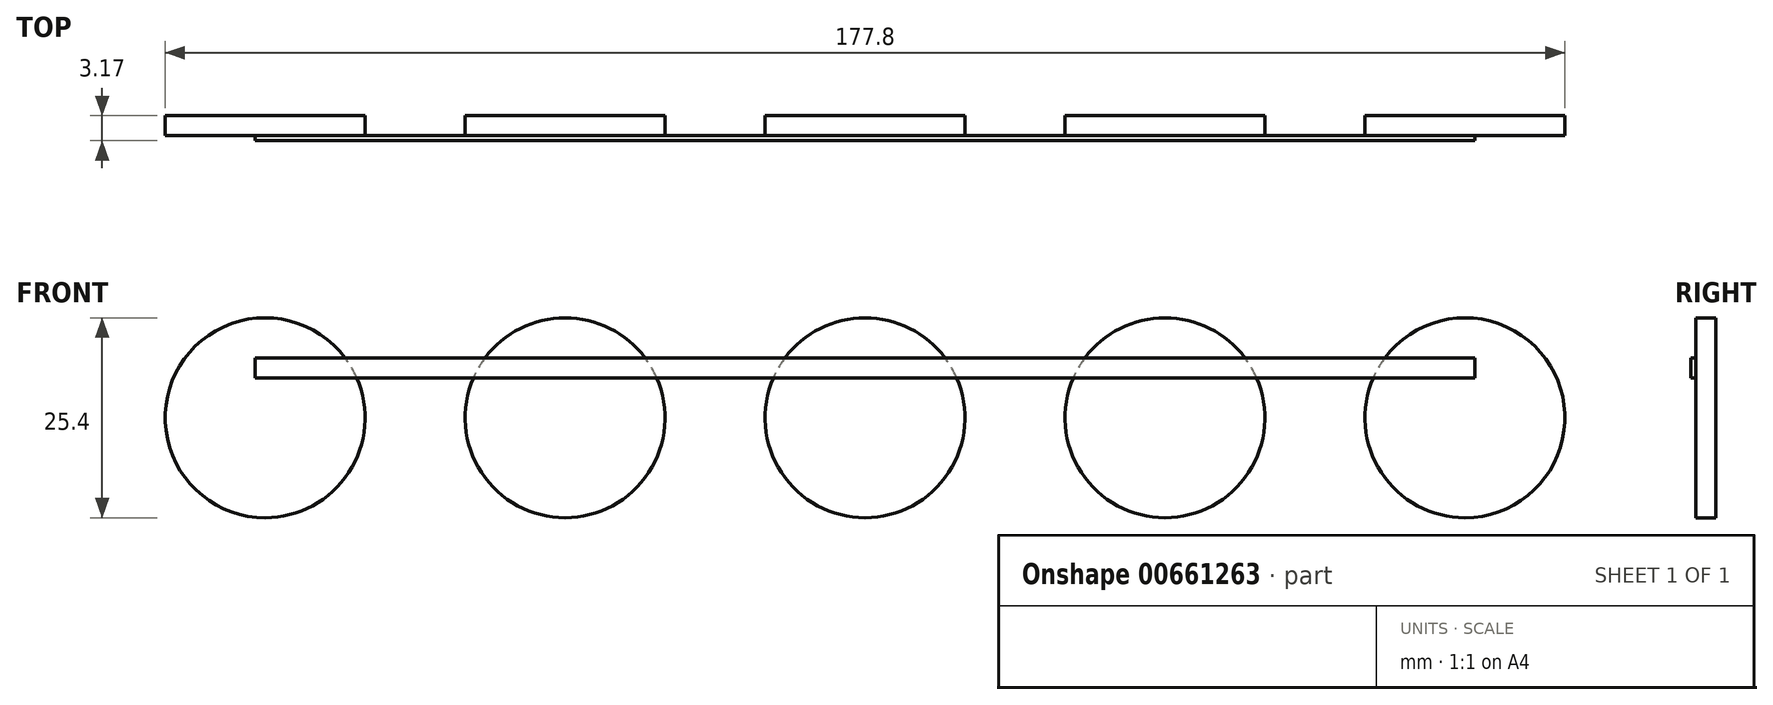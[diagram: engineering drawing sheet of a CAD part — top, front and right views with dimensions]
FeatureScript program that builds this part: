
annotation { "Feature Type Name" : "Feature", "Feature Type Description" : "" }
export const myFeature = defineFeature(function(context is Context, id is Id, definition is map)
    precondition{}
    {
        {
            var Q0;
            Q0=qCreatedBy(makeId("Front.planeOp"),FACE);
            var sketch = newSketch(context, id + "F0", { "sketchPlane" : qUnion([Q0])});
            skCircle(sketch, "E0", {"center": v(0, 0) * mm, "radius": 12.7 * mm});
            skCircle(sketch, "E1", {"center": v(38.1, 0) * mm, "radius": 12.7 * mm});
            skCircle(sketch, "E2", {"center": v(76.2, 0) * mm, "radius": 12.7 * mm});
            skCircle(sketch, "E3", {"center": v(-38.1, 0) * mm, "radius": 12.7 * mm});
            skCircle(sketch, "E4", {"center": v(-76.2, 0) * mm, "radius": 12.7 * mm});
            skSolve(sketch);
        }
        {
            var Q0;
            Q0=makeQuery(id+"F0.imprint","IMPRINT",FACE,{"disambiguationData":[TD([[makeQuery(id+"F0.imprint","IMPRINT",EDGE,{"derivedFrom":sQuery(id+"F0.wireOp",EDGE,"E4")}),1.0]])]});
            var Q1;
            Q1=makeQuery(id+"F0.imprint","IMPRINT",FACE,{"disambiguationData":[TD([[makeQuery(id+"F0.imprint","IMPRINT",EDGE,{"derivedFrom":sQuery(id+"F0.wireOp",EDGE,"E3")}),1.0]])]});
            var Q2;
            Q2=makeQuery(id+"F0.imprint","IMPRINT",FACE,{"disambiguationData":[TD([[makeQuery(id+"F0.imprint","IMPRINT",EDGE,{"derivedFrom":sQuery(id+"F0.wireOp",EDGE,"E0")}),1.0]])]});
            var Q3;
            Q3=makeQuery(id+"F0.imprint","IMPRINT",FACE,{"disambiguationData":[TD([[makeQuery(id+"F0.imprint","IMPRINT",EDGE,{"derivedFrom":sQuery(id+"F0.wireOp",EDGE,"E1")}),1.0]])]});
            var Q4;
            Q4=makeQuery(id+"F0.imprint","IMPRINT",FACE,{"disambiguationData":[TD([[makeQuery(id+"F0.imprint","IMPRINT",EDGE,{"derivedFrom":sQuery(id+"F0.wireOp",EDGE,"E2")}),1.0]])]});
            extrude(context, id + "F1", {"entities" : qUnion([Q0, Q1, Q2, Q3, Q4]), "depth" : 2.54 * mm, "offsetDistance" : 25.4 * mm});
        }
        {
            var Q0;
            Q0=makeQuery(id+"F1.opExtrude","CAP_FACE",FACE,{"disambiguationData":[OSD([sQuery(id+"F0.wireOp",EDGE,"E4")])],"isStart":false});
            var sketch = newSketch(context, id + "F2", { "sketchPlane" : qUnion([Q0])});
            skArc(sketch, "E5.0.0", {"start": v(-66.04, 7.62) * mm, "mid": v(-87.17, -6.4) * mm, "end": v(-64.56, 5.08) * mm});
            skPoint(sketch, "E6.0", {"position": v(-38.1, 0) * mm});
            skArc(sketch, "E7.0.0", {"start": v(-49.74, 5.08) * mm, "mid": v(-38.1, -12.7) * mm, "end": v(-26.46, 5.08) * mm});
            skPoint(sketch, "E8.0", {"position": v(0, 0) * mm});
            skArc(sketch, "E9.0.0", {"start": v(-11.64, 5.08) * mm, "mid": v(0, -12.7) * mm, "end": v(11.64, 5.08) * mm});
            skPoint(sketch, "E10.0", {"position": v(38.1, 0) * mm});
            skArc(sketch, "E11.0.0", {"start": v(26.46, 5.08) * mm, "mid": v(38.1, -12.7) * mm, "end": v(49.74, 5.08) * mm});
            skPoint(sketch, "E12.0", {"position": v(76.2, 0) * mm});
            skArc(sketch, "E13.0.0", {"start": v(64.56, 5.08) * mm, "mid": v(87.17, -6.4) * mm, "end": v(66.04, 7.62) * mm});
            skLineSegment(sketch, "E14", {"start": v(-76.2, 0) * mm, "end": v(-76.2, 12.7) * mm, "construction": true});
            skLineSegment(sketch, "E15", {"start": v(-38.1, 0) * mm, "end": v(-38.1, 12.7) * mm, "construction": true});
            skLineSegment(sketch, "E16", {"start": v(0, 0) * mm, "end": v(0, 12.7) * mm, "construction": true});
            skLineSegment(sketch, "E17", {"start": v(38.1, 0) * mm, "end": v(38.1, 12.7) * mm, "construction": true});
            skLineSegment(sketch, "E18", {"start": v(76.2, 0) * mm, "end": v(76.2, 12.7) * mm, "construction": true});
            skPoint(sketch, "E19", {"position": v(-76.2, 6.35) * mm});
            skLineSegment(sketch, "E20.bottom", {"start": v(-74.93, 7.62) * mm, "end": v(-77.47, 7.62) * mm, "construction": true});
            skLineSegment(sketch, "E20.top", {"start": v(-74.93, 5.08) * mm, "end": v(-77.47, 5.08) * mm, "construction": true});
            skLineSegment(sketch, "E20.left", {"start": v(-74.93, 7.62) * mm, "end": v(-74.93, 5.08) * mm, "construction": true});
            skLineSegment(sketch, "E20.right", {"start": v(-77.47, 7.62) * mm, "end": v(-77.47, 5.08) * mm, "construction": true});
            skPoint(sketch, "E21", {"position": v(-38.1, 6.35) * mm});
            skPoint(sketch, "E22", {"position": v(0, 6.35) * mm});
            skPoint(sketch, "E23", {"position": v(38.1, 6.35) * mm});
            skPoint(sketch, "E24", {"position": v(76.2, 6.35) * mm});
            skLineSegment(sketch, "E25.bottom", {"start": v(77.47, 7.62) * mm, "end": v(74.93, 7.62) * mm, "construction": true});
            skLineSegment(sketch, "E25.top", {"start": v(77.47, 5.08) * mm, "end": v(74.93, 5.08) * mm, "construction": true});
            skLineSegment(sketch, "E25.left", {"start": v(77.47, 7.62) * mm, "end": v(77.47, 5.08) * mm, "construction": true});
            skLineSegment(sketch, "E25.right", {"start": v(74.93, 7.62) * mm, "end": v(74.93, 5.08) * mm, "construction": true});
            skLineSegment(sketch, "E26.bottom", {"start": v(-77.47, 7.62) * mm, "end": v(77.47, 7.62) * mm});
            skLineSegment(sketch, "E26.top", {"start": v(-77.47, 5.08) * mm, "end": v(77.47, 5.08) * mm});
            skLineSegment(sketch, "E26.left", {"start": v(-77.47, 7.62) * mm, "end": v(-77.47, 5.08) * mm});
            skLineSegment(sketch, "E26.right", {"start": v(77.47, 7.62) * mm, "end": v(77.47, 5.08) * mm});
            skArc(sketch, "E27.trimOffspring", {"start": v(-27.94, 7.62) * mm, "mid": v(-38.1, 12.7) * mm, "end": v(-48.26, 7.62) * mm});
            skArc(sketch, "E28.trimOffspring", {"start": v(10.16, 7.62) * mm, "mid": v(0, 12.7) * mm, "end": v(-10.16, 7.62) * mm});
            skArc(sketch, "E29.trimOffspring", {"start": v(48.26, 7.62) * mm, "mid": v(38.1, 12.7) * mm, "end": v(27.94, 7.62) * mm});
            skSolve(sketch);
        }
        {
            var Q0;
            {var subQ10=sQuery(id+"F2.wireOp",EDGE,"E26.right");Q0=makeQuery(id+"F2.imprint","IMPRINT",FACE,{"disambiguationData":[TD([[makeQuery(id+"F2.imprint","IMPRINT",EDGE,{"derivedFrom":subQ10}),-1.0]])]});}
            var Q1;
            {var subQ4=sQuery(id+"F2.wireOp",EDGE,"E26.left");Q1=makeQuery(id+"F2.imprint","IMPRINT",FACE,{"disambiguationData":[TD([[makeQuery(id+"F2.imprint","IMPRINT",EDGE,{"derivedFrom":subQ4}),1.0]])]});}
            extrude(context, id + "F3", {"entities" : qUnion([Q0, Q1]), "depth" : 0.64 * mm, "offsetDistance" : 25.4 * mm});
        }
    });
